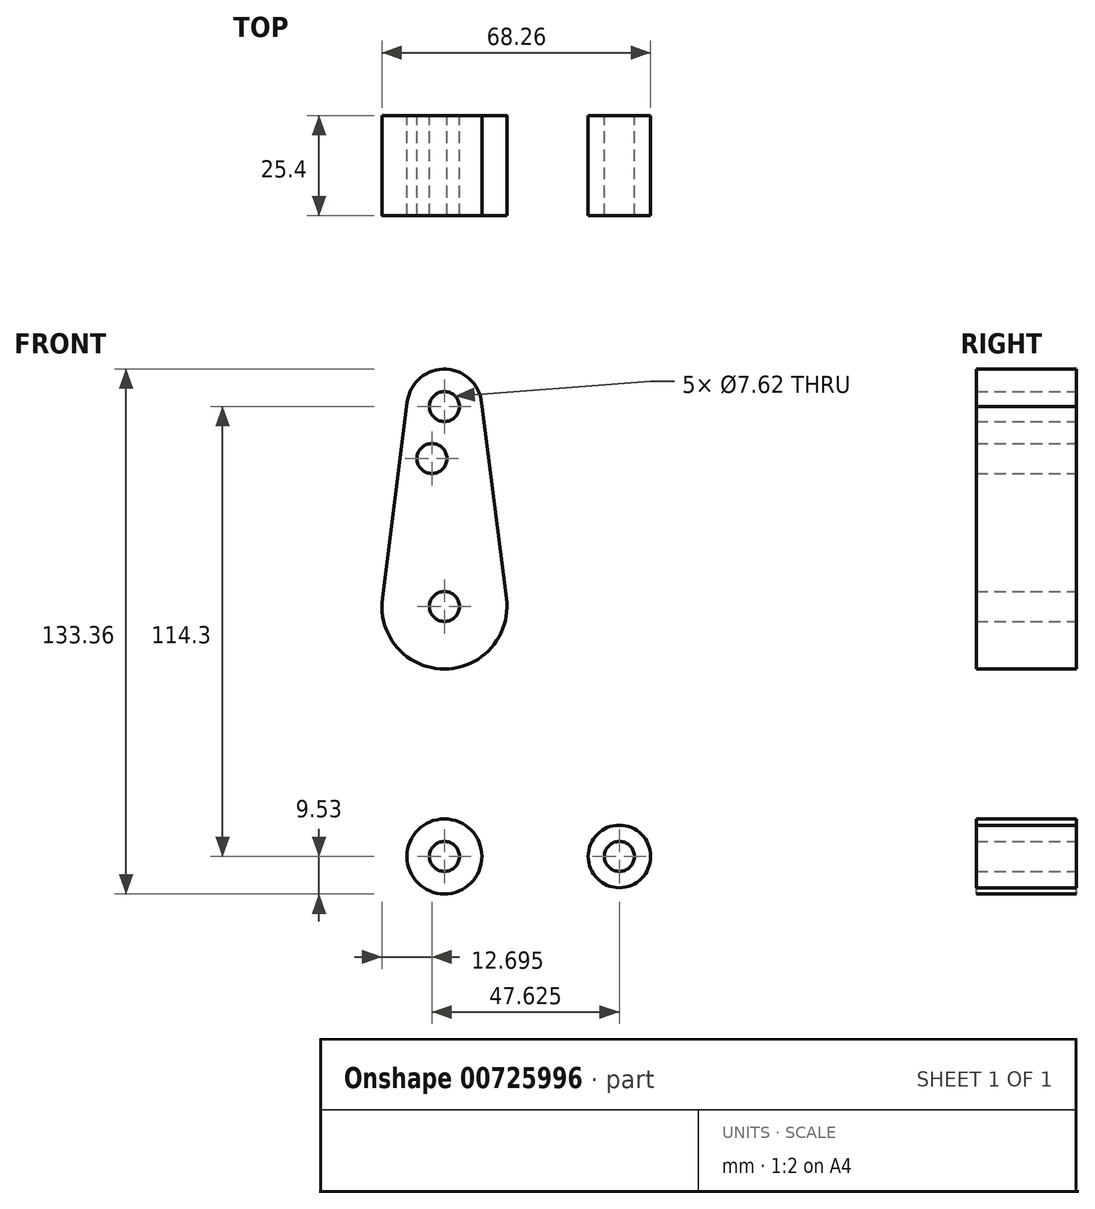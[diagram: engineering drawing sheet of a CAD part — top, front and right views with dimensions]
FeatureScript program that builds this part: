
annotation { "Feature Type Name" : "Feature", "Feature Type Description" : "" }
export const myFeature = defineFeature(function(context is Context, id is Id, definition is map)
    precondition{}
    {
        {
            var Q0;
            Q0=qCreatedBy(makeId("Front.planeOp"),FACE);
            var sketch = newSketch(context, id + "F0", { "sketchPlane" : qUnion([Q0])});
            skLineSegment(sketch, "E0", {"start": v(0, 0) * mm, "end": v(0, 114.3) * mm, "construction": true});
            skLineSegment(sketch, "E1", {"start": v(0, 0) * mm, "end": v(44.45, 0) * mm, "construction": true});
            skCircle(sketch, "E2", {"center": v(0, 114.3) * mm, "radius": 9.53 * mm});
            skCircle(sketch, "E3", {"center": v(44.45, 0) * mm, "radius": 7.94 * mm});
            skCircle(sketch, "E4", {"center": v(0, 63.5) * mm, "radius": 15.88 * mm});
            skCircle(sketch, "E5", {"center": v(0, 0) * mm, "radius": 9.53 * mm});
            skLineSegment(sketch, "E6", {"start": v(-9.45, 115.5) * mm, "end": v(-15.75, 65.48) * mm});
            skLineSegment(sketch, "E7", {"start": v(9.53, 114.3) * mm, "end": v(15.75, 65.5) * mm});
            skLineSegment(sketch, "E8", {"start": v(0, -9.53) * mm, "end": v(44.73, -7.93) * mm});
            skLineSegment(sketch, "E9", {"start": v(0, 9.53) * mm, "end": v(0.68, 9.5) * mm});
            skArc(sketch, "E10", {"start": v(11.2, 16.23) * mm, "mid": v(12.82, 11.18) * mm, "end": v(17.6, 8.9) * mm});
            skLineSegment(sketch, "E11.trimOffspring", {"start": v(11.2, 16.23) * mm, "end": v(15.75, 61.44) * mm});
            skLineSegment(sketch, "E12.trimOffspring", {"start": v(17.6, 8.9) * mm, "end": v(44.73, 7.93) * mm});
            skCircle(sketch, "E13", {"center": v(0, 63.5) * mm, "radius": 3.81 * mm});
            skCircle(sketch, "E14", {"center": v(0, 0) * mm, "radius": 3.81 * mm});
            skCircle(sketch, "E15", {"center": v(0, 114.3) * mm, "radius": 3.81 * mm});
            skCircle(sketch, "E16", {"center": v(44.45, 0) * mm, "radius": 3.81 * mm});
            skCircle(sketch, "E17", {"center": v(-3.18, 101.1) * mm, "radius": 3.81 * mm});
            skLineSegment(sketch, "E18", {"start": v(-15.8, 61.91) * mm, "end": v(-9.57, 0) * mm});
            skSolve(sketch);
        }
        {
            var Q0;
            Q0 = qSketchRegion(id + "F0", true);
            extrude(context, id + "F1", {"entities" : qUnion([Q0]), "depth" : 25.4 * mm, "offsetDistance" : 25.4 * mm});
        }
    });
